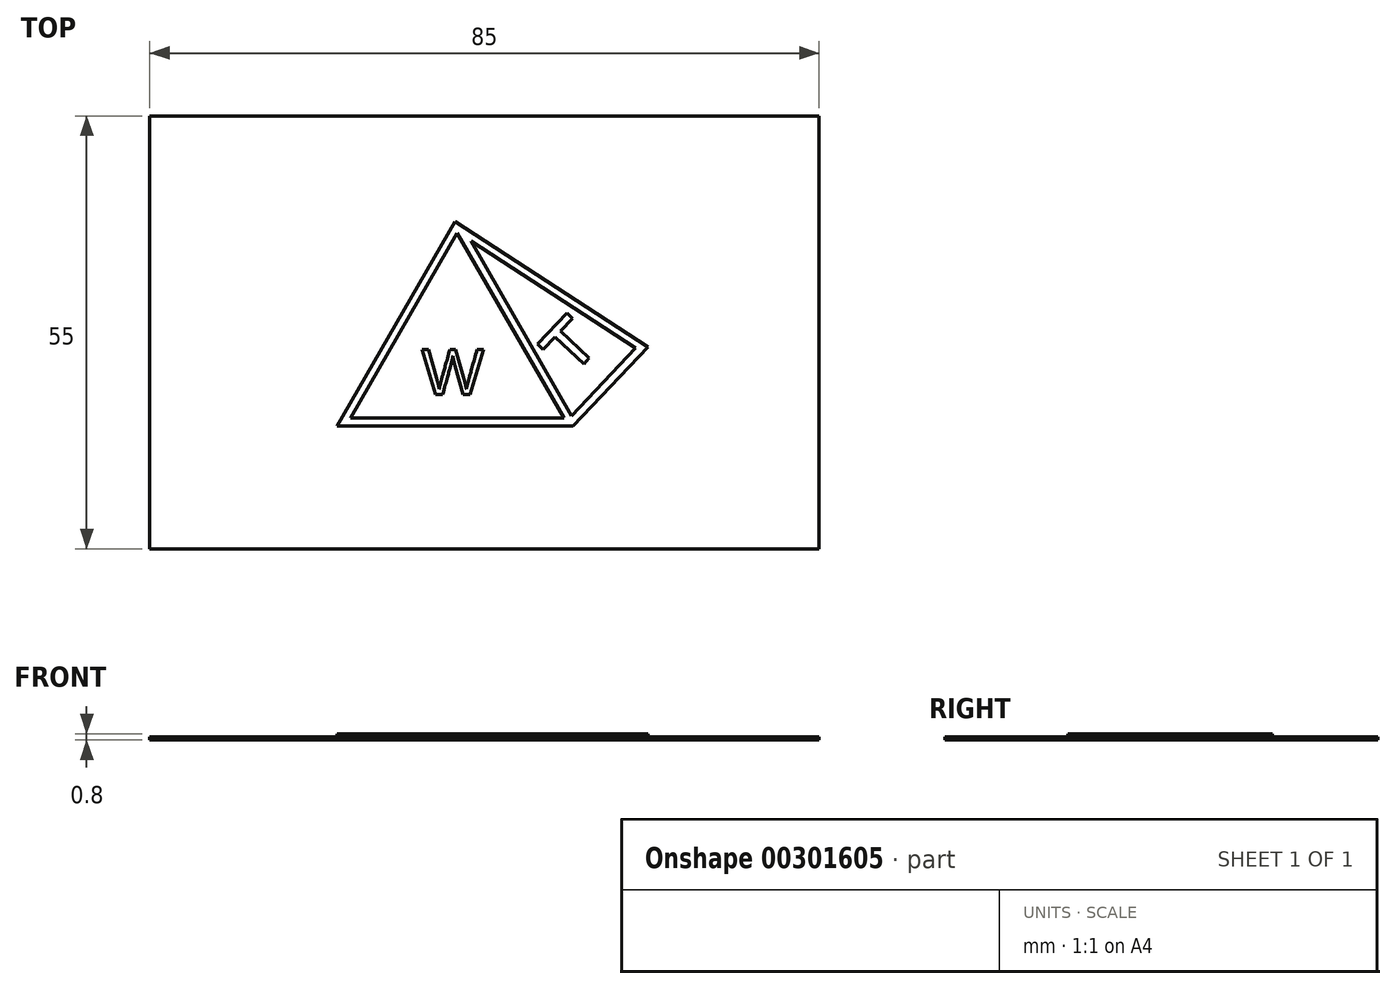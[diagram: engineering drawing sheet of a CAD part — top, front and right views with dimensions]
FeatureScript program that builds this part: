
annotation { "Feature Type Name" : "Feature", "Feature Type Description" : "" }
export const myFeature = defineFeature(function(context is Context, id is Id, definition is map)
    precondition{}
    {
        {
            var Q0;
            Q0=qCreatedBy(makeId("Top.planeOp"),FACE);
            var sketch = newSketch(context, id + "F0", { "sketchPlane" : qUnion([Q0])});
            skLineSegment(sketch, "E0.bottom", {"start": v(-42.5, 27.5) * mm, "end": v(42.5, 27.5) * mm});
            skLineSegment(sketch, "E0.top", {"start": v(-42.5, -27.5) * mm, "end": v(42.5, -27.5) * mm});
            skLineSegment(sketch, "E0.left", {"start": v(-42.5, 27.5) * mm, "end": v(-42.5, -27.5) * mm});
            skLineSegment(sketch, "E0.right", {"start": v(42.5, 27.5) * mm, "end": v(42.5, -27.5) * mm});
            skSolve(sketch);
        }
        {
            var Q0;
            Q0 = qSketchRegion(id + "F0", true);
            extrude(context, id + "F1", {"entities" : qUnion([Q0]), "depth" : 0.4 * mm});
        }
        {
            var Q0;
            Q0=makeQuery(id+"F1.opExtrude","CAP_FACE",FACE,{"disambiguationData":[OSD([sQuery(id+"F0.wireOp",EDGE,"E0.bottom"),sQuery(id+"F0.wireOp",EDGE,"E0.top"),sQuery(id+"F0.wireOp",EDGE,"E0.left"),sQuery(id+"F0.wireOp",EDGE,"E0.right")])],"isStart":false});
            var sketch = newSketch(context, id + "F2", { "sketchPlane" : qUnion([Q0])});
            skLineSegment(sketch, "E1", {"start": v(-3.74, 14.1) * mm, "end": v(-18.74, -11.9) * mm});
            skLineSegment(sketch, "E2", {"start": v(-18.74, -11.9) * mm, "end": v(11.26, -11.9) * mm});
            skLineSegment(sketch, "E3", {"start": v(-3.74, 19.74) * mm, "end": v(-3.74, -32.87) * mm, "construction": true});
            skLineSegment(sketch, "E4.1", {"start": v(-17, -10.9) * mm, "end": v(6.39, -10.9) * mm});
            skLineSegment(sketch, "E4.2", {"start": v(-6.6, 7.14) * mm, "end": v(-17, -10.9) * mm});
            skLineSegment(sketch, "E5", {"start": v(11.26, -11.9) * mm, "end": v(20.77, -1.84) * mm});
            skLineSegment(sketch, "E6", {"start": v(20.77, -1.84) * mm, "end": v(-3.74, 14.1) * mm});
            skLineSegment(sketch, "E7.0", {"start": v(19.21, -2.02) * mm, "end": v(-1.71, 11.58) * mm});
            skLineSegment(sketch, "E7.1", {"start": v(11.1, -10.6) * mm, "end": v(19.21, -2.02) * mm});
            skLineSegment(sketch, "E8.0", {"start": v(11.1, -10.6) * mm, "end": v(-1.71, 11.58) * mm});
            skLineSegment(sketch, "E9", {"start": v(6.39, -10.9) * mm, "end": v(10.1, -10.9) * mm});
            skLineSegment(sketch, "E10.trimOffspring", {"start": v(10.1, -10.9) * mm, "end": v(-3.45, 12.6) * mm});
            skLineSegment(sketch, "E11", {"start": v(-6.6, 7.14) * mm, "end": v(-3.45, 12.6) * mm});
            skSolve(sketch);
        }
        {
            var Q0;
            Q0 = qSketchRegion(id + "F2", true);
            extrude(context, id + "F3", {"entities" : qUnion([Q0]), "operationType" : NewBodyOperationType.ADD, "depth" : 0.4 * mm});
        }
        {
            var Q0;
            {var subQ0=sQuery(id+"F0.wireOp",EDGE,"E0.left");var subQ1=sQuery(id+"F0.wireOp",EDGE,"E0.top");var subQ2=sQuery(id+"F0.wireOp",EDGE,"E0.right");var subQ3=sQuery(id+"F0.wireOp",EDGE,"E0.bottom");Q0=makeQuery(id+"F3.boolean.opBoolean","SPLIT",FACE,{"disambiguationData":[TD([makeQuery(id+"F1.opExtrude","SWEPT_FACE",FACE,{"disambiguationData":[OSD([subQ3])]})])],"derivedFrom":makeQuery(id+"F1.opExtrude","CAP_FACE",FACE,{"disambiguationData":[OSD([subQ3,subQ1,subQ0,subQ2])],"isStart":false})});}
            var sketch = newSketch(context, id + "F4", { "sketchPlane" : qUnion([Q0])});
            skPoint(sketch, "E12", {"position": v(-11.24, 1.1) * mm});
            skLineSegment(sketch, "E13", {"start": v(11.26, -11.9) * mm, "end": v(-3.74, 14.1) * mm, "construction": true});
            skLineSegment(sketch, "E14", {"start": v(12.97, -3.66) * mm, "end": v(13.31, -3.3) * mm});
            skLineSegment(sketch, "E15", {"start": v(13.31, -3.3) * mm, "end": v(9.68, 0.14) * mm});
            skLineSegment(sketch, "E16", {"start": v(9.68, 0.14) * mm, "end": v(11.2, 1.75) * mm});
            skLineSegment(sketch, "E17", {"start": v(11.2, 1.75) * mm, "end": v(10.47, 2.44) * mm});
            skLineSegment(sketch, "E18", {"start": v(10.47, 2.44) * mm, "end": v(8.6, 0.47) * mm});
            skLineSegment(sketch, "E19", {"start": v(12.97, -3.66) * mm, "end": v(6.2, 2.74) * mm, "construction": true});
            skLineSegment(sketch, "E20.MirrorCS", {"start": v(6.75, -1.5) * mm, "end": v(8.6, 0.47) * mm});
            skLineSegment(sketch, "E21.MirrorCS", {"start": v(7.47, -2.2) * mm, "end": v(6.75, -1.5) * mm});
            skLineSegment(sketch, "E22.MirrorCS", {"start": v(9, -0.58) * mm, "end": v(7.47, -2.2) * mm});
            skLineSegment(sketch, "E23.MirrorCS", {"start": v(12.97, -3.66) * mm, "end": v(12.63, -4.02) * mm});
            skLineSegment(sketch, "E24.MirrorCS", {"start": v(12.63, -4.02) * mm, "end": v(9, -0.58) * mm});
            skText(sketch, "E25", { "text": "W", "fontName": "Arimo-Regular.ttf"});
            skLineSegment(sketch, "E26", {"start": v(-3.74, 14.1) * mm, "end": v(-3.74, -32.76) * mm, "construction": true});
            const initialGuessF4  = {"E25": [-0.00795, -0.0079, 1, 0, 0.006]};
            skSetInitialGuess(sketch, initialGuessF4);
            skSolve(sketch);
        }
        {
            var Q0;
            Q0 = qSketchRegion(id + "F4", true);
            extrude(context, id + "F5", {"entities" : qUnion([Q0]), "operationType" : NewBodyOperationType.ADD, "depth" : 0.4 * mm});
        }
    });
